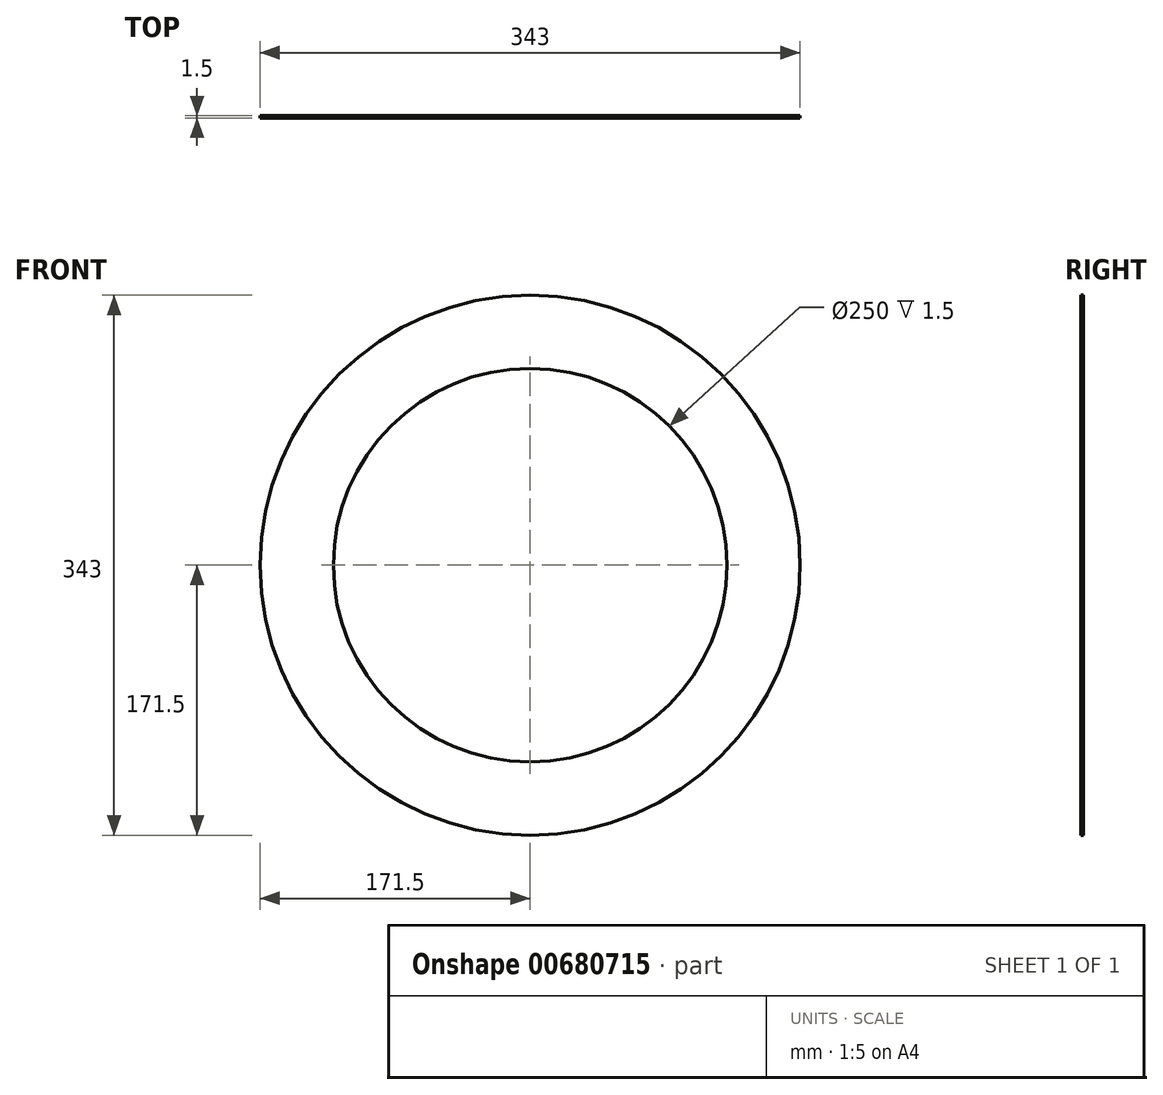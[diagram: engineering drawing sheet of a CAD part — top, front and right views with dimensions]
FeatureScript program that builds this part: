
annotation { "Feature Type Name" : "Feature", "Feature Type Description" : "" }
export const myFeature = defineFeature(function(context is Context, id is Id, definition is map)
    precondition{}
    {
        {
            var Q0;
            Q0=qCreatedBy(makeId("Front.planeOp"),FACE);
            var sketch = newSketch(context, id + "F0", { "sketchPlane" : qUnion([Q0])});
            skCircle(sketch, "E0", {"center": v(0, 0) * mm, "radius": 125 * mm});
            skCircle(sketch, "E1", {"center": v(0, 0) * mm, "radius": 171.5 * mm});
            skSolve(sketch);
        }
        {
            var Q0;
            Q0 = qSketchRegion(id + "F0", true);
            extrude(context, id + "F1", {"entities" : qUnion([Q0]), "depth" : 1.5 * mm, "offsetDistance" : 25 * mm});
        }
    });
